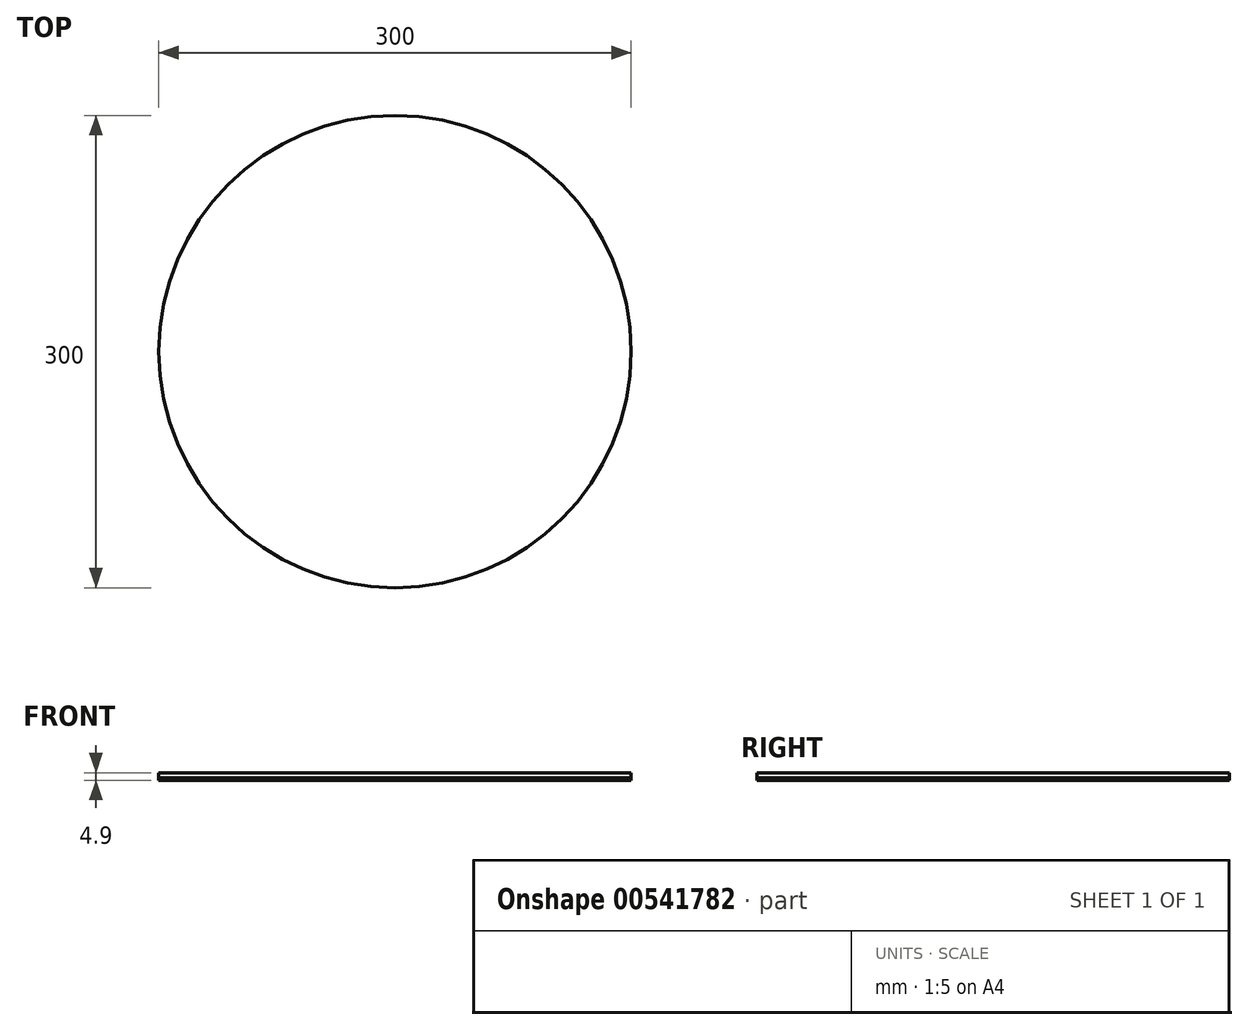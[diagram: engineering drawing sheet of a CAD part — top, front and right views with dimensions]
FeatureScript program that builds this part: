
annotation { "Feature Type Name" : "Feature", "Feature Type Description" : "" }
export const myFeature = defineFeature(function(context is Context, id is Id, definition is map)
    precondition{}
    {
        {
            var Q0;
            Q0=qCreatedBy(makeId("Top.planeOp"),FACE);
            var sketch = newSketch(context, id + "F0", { "sketchPlane" : qUnion([Q0])});
            skCircle(sketch, "E0", {"center": v(0, 0) * mm, "radius": 150 * mm});
            skSolve(sketch);
        }
        {
            var Q0;
            Q0=makeQuery(id+"F0.imprint","IMPRINT",FACE,{"disambiguationData":[TD([[makeQuery(id+"F0.imprint","IMPRINT",EDGE,{"derivedFrom":sQuery(id+"F0.wireOp",EDGE,"E0")}),1.0]])]});
            extrude(context, id + "F1", {"entities" : qUnion([Q0]), "depth" : 3.3 * mm, "offsetDistance" : 25 * mm});
        }
        {
            var Q0;
            Q0=makeQuery(id+"F0.imprint","IMPRINT",FACE,{"disambiguationData":[TD([[makeQuery(id+"F0.imprint","IMPRINT",EDGE,{"derivedFrom":sQuery(id+"F0.wireOp",EDGE,"E0")}),1.0]])]});
            extrude(context, id + "F2", {"entities" : qUnion([Q0]), "oppositeDirection" : true, "depth" : 1.6 * mm, "offsetDistance" : 25 * mm});
        }
    });
